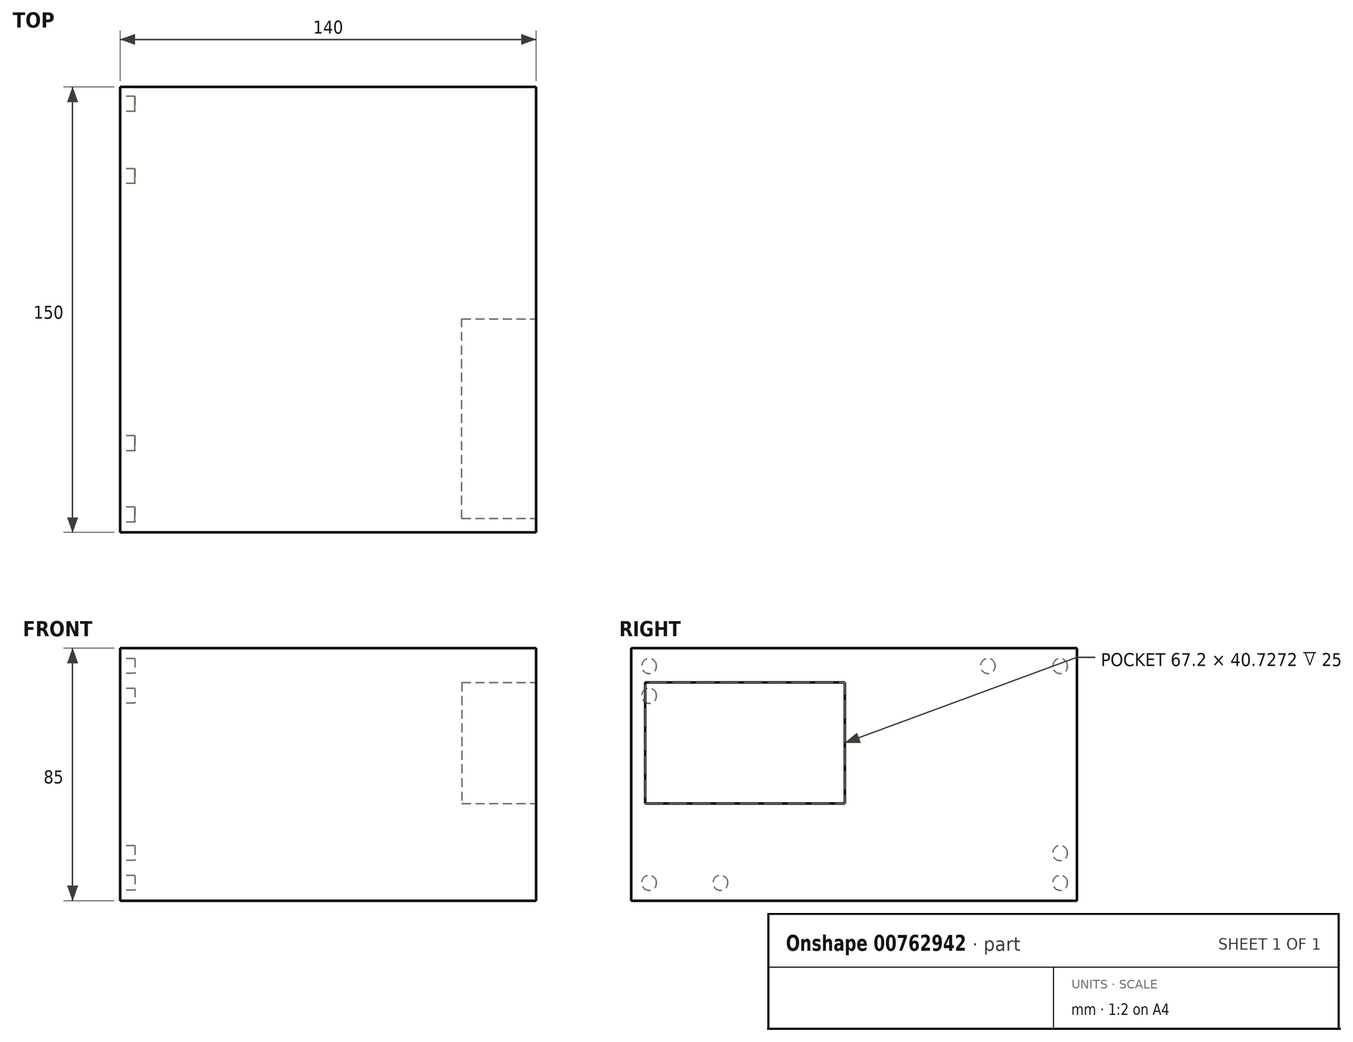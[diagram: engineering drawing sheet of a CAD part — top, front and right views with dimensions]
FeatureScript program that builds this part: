
annotation { "Feature Type Name" : "Feature", "Feature Type Description" : "" }
export const myFeature = defineFeature(function(context is Context, id is Id, definition is map)
    precondition{}
    {
        {
            var Q0;
            Q0=qCreatedBy(makeId("Top.planeOp"),FACE);
            var sketch = newSketch(context, id + "F0", { "sketchPlane" : qUnion([Q0])});
            skLineSegment(sketch, "E0.bottom", {"start": v(-85.45, -77.44) * mm, "end": v(54.55, -77.44) * mm});
            skLineSegment(sketch, "E0.top", {"start": v(-85.45, 72.56) * mm, "end": v(54.55, 72.56) * mm});
            skLineSegment(sketch, "E0.left", {"start": v(-85.45, -77.44) * mm, "end": v(-85.45, 72.56) * mm});
            skLineSegment(sketch, "E0.right", {"start": v(54.55, -77.44) * mm, "end": v(54.55, 72.56) * mm});
            skSolve(sketch);
        }
        {
            var Q0;
            Q0=makeQuery(id+"F0.imprint","IMPRINT",FACE,{"disambiguationData":[TD([[makeQuery(id+"F0.imprint","IMPRINT",EDGE,{"derivedFrom":sQuery(id+"F0.wireOp",EDGE,"E0.bottom")}),1.0]])]});
            extrude(context, id + "F1", {"entities" : qUnion([Q0]), "depth" : 85 * mm, "offsetDistance" : 25 * mm});
        }
        {
            var Q0;
            Q0=makeQuery(id+"F1.opExtrude","SWEPT_FACE",FACE,{"disambiguationData":[OSD([sQuery(id+"F0.wireOp",EDGE,"E0.right")])]});
            var sketch = newSketch(context, id + "F2", { "sketchPlane" : qUnion([Q0])});
            skLineSegment(sketch, "E1.bottom", {"start": v(-72.74, 73.47) * mm, "end": v(-5.54, 73.47) * mm});
            skLineSegment(sketch, "E1.top", {"start": v(-72.74, 32.75) * mm, "end": v(-5.54, 32.75) * mm});
            skLineSegment(sketch, "E1.left", {"start": v(-72.74, 73.47) * mm, "end": v(-72.74, 32.75) * mm});
            skLineSegment(sketch, "E1.right", {"start": v(-5.54, 73.47) * mm, "end": v(-5.54, 32.75) * mm});
            skSolve(sketch);
        }
        {
            var Q0;
            Q0=makeQuery(id+"F2.imprint","IMPRINT",FACE,{"disambiguationData":[TD([[makeQuery(id+"F2.imprint","IMPRINT",EDGE,{"derivedFrom":sQuery(id+"F2.wireOp",EDGE,"E1.bottom")}),-1.0]])]});
            extrude(context, id + "F3", {"entities" : qUnion([Q0]), "operationType" : NewBodyOperationType.REMOVE, "oppositeDirection" : true, "depth" : 25 * mm, "offsetDistance" : 25 * mm});
        }
        {
            var Q0;
            Q0=makeQuery(id+"F1.opExtrude","SWEPT_FACE",FACE,{"disambiguationData":[OSD([sQuery(id+"F0.wireOp",EDGE,"E0.left")])]});
            var sketch = newSketch(context, id + "F4", { "sketchPlane" : qUnion([Q0])});
            skCircle(sketch, "E2", {"center": v(-66.88, 79) * mm, "radius": 2.5 * mm});
            skCircle(sketch, "E3", {"center": v(-42.56, 79) * mm, "radius": 2.5 * mm});
            skCircle(sketch, "E4", {"center": v(-66.88, 16) * mm, "radius": 2.5 * mm});
            skCircle(sketch, "E5", {"center": v(-66.88, 6) * mm, "radius": 2.5 * mm});
            skCircle(sketch, "E6", {"center": v(71.44, 6) * mm, "radius": 2.5 * mm});
            skCircle(sketch, "E7", {"center": v(47.44, 6) * mm, "radius": 2.5 * mm});
            skCircle(sketch, "E8", {"center": v(71.44, 79) * mm, "radius": 2.5 * mm});
            skCircle(sketch, "E9", {"center": v(71.44, 69) * mm, "radius": 2.5 * mm});
            skSolve(sketch);
        }
        {
            var Q0;
            Q0=makeQuery(id+"F4.imprint","IMPRINT",FACE,{"disambiguationData":[TD([[makeQuery(id+"F4.imprint","IMPRINT",EDGE,{"derivedFrom":sQuery(id+"F4.wireOp",EDGE,"E2")}),1.0]])]});
            var Q1;
            Q1=makeQuery(id+"F4.imprint","IMPRINT",FACE,{"disambiguationData":[TD([[makeQuery(id+"F4.imprint","IMPRINT",EDGE,{"derivedFrom":sQuery(id+"F4.wireOp",EDGE,"E3")}),1.0]])]});
            var Q2;
            Q2=makeQuery(id+"F4.imprint","IMPRINT",FACE,{"disambiguationData":[TD([[makeQuery(id+"F4.imprint","IMPRINT",EDGE,{"derivedFrom":sQuery(id+"F4.wireOp",EDGE,"E4")}),1.0]])]});
            var Q3;
            Q3=makeQuery(id+"F4.imprint","IMPRINT",FACE,{"disambiguationData":[TD([[makeQuery(id+"F4.imprint","IMPRINT",EDGE,{"derivedFrom":sQuery(id+"F4.wireOp",EDGE,"E5")}),1.0]])]});
            var Q4;
            Q4=makeQuery(id+"F4.imprint","IMPRINT",FACE,{"disambiguationData":[TD([[makeQuery(id+"F4.imprint","IMPRINT",EDGE,{"derivedFrom":sQuery(id+"F4.wireOp",EDGE,"E7")}),1.0]])]});
            var Q5;
            Q5=makeQuery(id+"F4.imprint","IMPRINT",FACE,{"disambiguationData":[TD([[makeQuery(id+"F4.imprint","IMPRINT",EDGE,{"derivedFrom":sQuery(id+"F4.wireOp",EDGE,"E6")}),1.0]])]});
            var Q6;
            Q6=makeQuery(id+"F4.imprint","IMPRINT",FACE,{"disambiguationData":[TD([[makeQuery(id+"F4.imprint","IMPRINT",EDGE,{"derivedFrom":sQuery(id+"F4.wireOp",EDGE,"E8")}),1.0]])]});
            var Q7;
            Q7=makeQuery(id+"F4.imprint","IMPRINT",FACE,{"disambiguationData":[TD([[makeQuery(id+"F4.imprint","IMPRINT",EDGE,{"derivedFrom":sQuery(id+"F4.wireOp",EDGE,"E9")}),1.0]])]});
            extrude(context, id + "F5", {"entities" : qUnion([Q0, Q1, Q2, Q3, Q4, Q5, Q6, Q7]), "operationType" : NewBodyOperationType.REMOVE, "oppositeDirection" : true, "depth" : 5 * mm, "offsetDistance" : 25 * mm});
        }
    });
